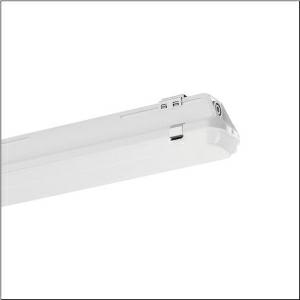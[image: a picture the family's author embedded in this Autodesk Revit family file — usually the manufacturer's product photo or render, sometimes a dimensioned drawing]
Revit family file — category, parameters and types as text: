
# Revit family: monsun_11_emergency_51fp207p437l3g
name_source: partatom
category: Lighting Fixtures
units: mm (PartAtom-declared; Revit-internal decimal feet)

## family parameters
Cut with Voids When Loaded = No
Host = Face
Light Source = No
Part Type = Normal
Room Calculation Point = No
Round Connector Dimension = Use Diameter
Shared = No

## types (1)
- --- (1 x LED, 890 lm, 6.4 W, 4000K)
    Apparent Load = 6 VA
    CIE Flux Codes = 45 75 93 94 100
    Color Rendering = 80
    Color Temperature = 4000K
    Default Elevation = 1800 mm
    Description = Monsun 11 emergency, damp-proof luminaire, chain hanger, primary optical cover: enclosure, of PC, light emission: direct distribution, primary light characteristic: symmetric, installation type: suspended mounting, surface-mounted, horizontal mounting, vertical mounting, LED, rated luminous flux: 3.990lm, luminous efficacy: 164lm/W, light colour: 840, colour temperature: 4000K, control gear: ON/OFF, with terminal, 4-pole, max. 2.5mm², mains connection: 220..240V, AC, 50/60Hz, rated input power: 28W, control gear: single battery element, battery: LiFePO4, 9Ah, luminaire housing, of glass-fibre reinforced polyester, uncoated, bright grey, incl. chain hanger, length: 1.590mm, width: 90mm, height: 88mm, clip for enclosure, of stainless steel (V2A), ceiling mounting element, of stainless steel (V2A), chain hanger, of stainless steel (V2A), protection rating (complete): IP66, insulation class (complete): insulation class I (protective earthing), certification: CE, UKCA, protection symbol: D, impact resistance: IK08, permissible operating ambient temperature: +5..+35°C, standard: EN 50419, EN 60598-2-1, EN 60598-2-22, contact your sales advisor before using the luminaires in applications with unclear chemical exposure, large temperature fluctuations or condensation-forming humidity, LABS conformity tested according to VDMA 24364:2018-05, no direct snow, no direct sun, no direct rain, for indoor or canopied outdoor use, corresponds to IFS (International Featured Standards) requirements for safety and quality in the food industry, packaging unit: 1 piece
    Height = 89 mm
    Lamp = 1 x LED
    Lamp Light Flux = 890 lm
    Lamp Power = 6.4 W
    Lamp count = 1
    Length = 1590 mm
    Luminous efficacy = 139 lm/W
    Manufacturer = Siteco
    ModVariant = No
    Model = 51FP207P437L3G
    Mounting Place = Ceiling
    Mounting Type = Surface mounted
    Number of Poles = 1
    OnlyDefault = Yes
    Power Factor = 1
    Product Name = Monsun 11 emergency
    Product group = damp-proof luminaire
    ProductGroupID = 300
    Protection Class = Protection class I
    Protection Degree = IP 66
    RLX_Detail_Level = 1
    RLX_Emergency_Light_Flux = 0 lm
    RLX_Emergency_Type = 0
    RLX_Emergency_Type_DB = No
    RlxData = <blob elided: 88729 chars, md5=1af34947>
    Socket = socket
    Standby Power = 0 W
    System Light Flux = 890 lm
    System Power = 6 W
    Type Comments = : emergency light operation: 3 h
    Type Image = l_1349237.jpg
    URL = http://relux.com
    VarID = @adj_034293
    Voltage = 0 V
    Weight = 0.00 kg
    Width = 90 mm

## geometry (parser evidence)
native form markers: Blend x4, Sweep x12
no freeform markers — native parametric forms only
